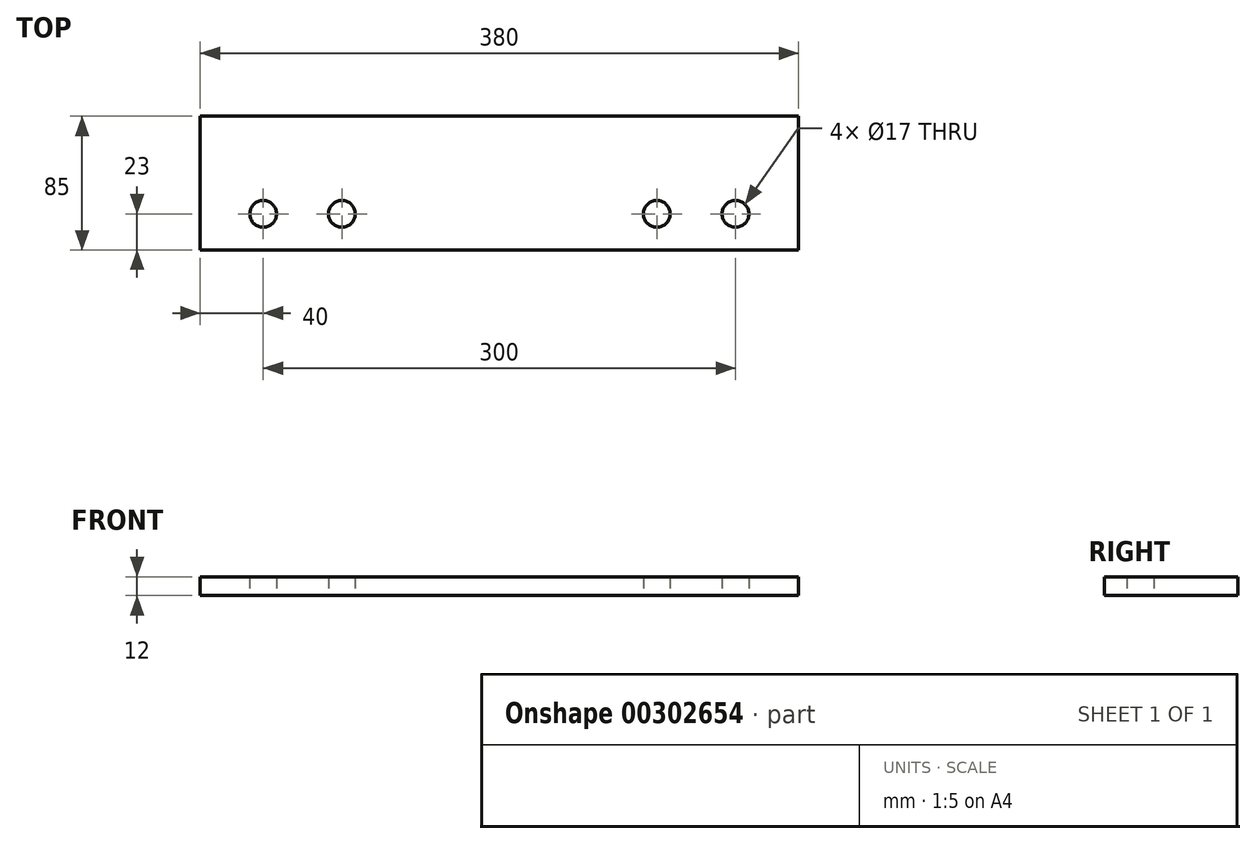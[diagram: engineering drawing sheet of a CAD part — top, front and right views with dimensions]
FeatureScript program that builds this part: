
annotation { "Feature Type Name" : "Feature", "Feature Type Description" : "" }
export const myFeature = defineFeature(function(context is Context, id is Id, definition is map)
    precondition{}
    {
        {
            var Q0;
            Q0=qCreatedBy(makeId("Top.planeOp"),FACE);
            var sketch = newSketch(context, id + "F0", { "sketchPlane" : qUnion([Q0])});
            skLineSegment(sketch, "E0.bottom", {"start": v(0, 0) * mm, "end": v(380, 0) * mm});
            skLineSegment(sketch, "E0.top", {"start": v(0, 85) * mm, "end": v(380, 85) * mm});
            skLineSegment(sketch, "E0.left", {"start": v(0, 0) * mm, "end": v(0, 85) * mm});
            skLineSegment(sketch, "E0.right", {"start": v(380, 0) * mm, "end": v(380, 85) * mm});
            skLineSegment(sketch, "E1", {"start": v(190, 125.6) * mm, "end": v(190, -230.75) * mm});
            skCircle(sketch, "E2", {"center": v(290, 23) * mm, "radius": 8.5 * mm});
            skCircle(sketch, "E3", {"center": v(340, 23) * mm, "radius": 8.5 * mm});
            skCircle(sketch, "E4.MirrorC", {"center": v(90, 23) * mm, "radius": 8.5 * mm});
            skCircle(sketch, "E5.MirrorC", {"center": v(40, 23) * mm, "radius": 8.5 * mm});
            skSolve(sketch);
        }
        {
            var Q0;
            Q0=qSketchRegion(id+"F0",true);
            extrude(context, id + "F1", {"entities" : qUnion([Q0]), "depth" : 12 * mm});
        }
    });
